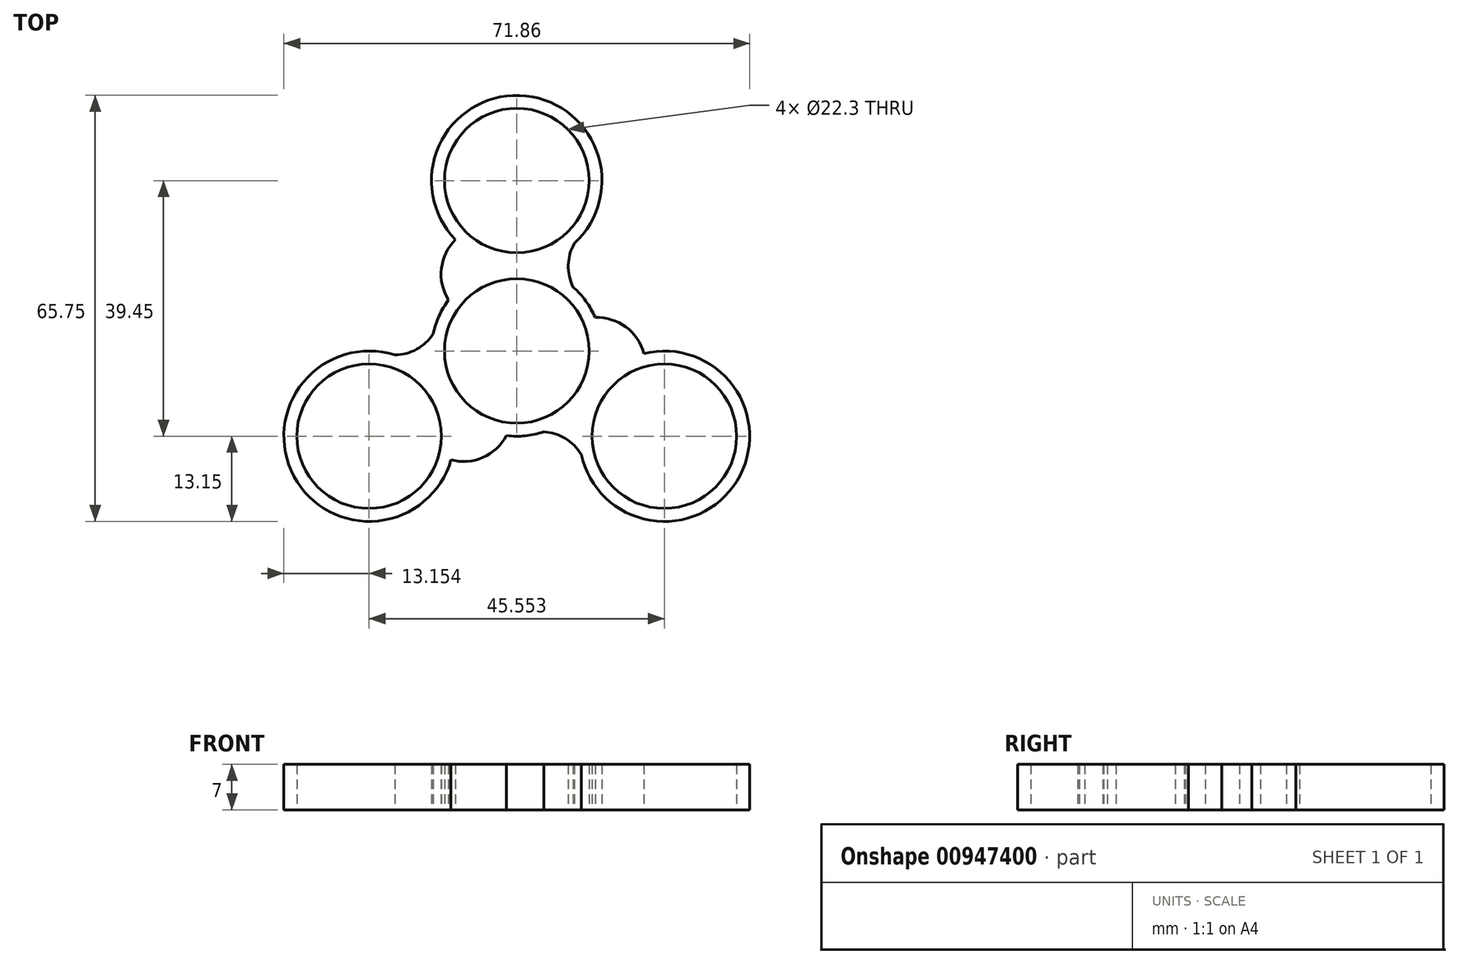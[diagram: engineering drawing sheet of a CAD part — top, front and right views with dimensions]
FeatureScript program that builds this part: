
annotation { "Feature Type Name" : "Feature", "Feature Type Description" : "" }
export const myFeature = defineFeature(function(context is Context, id is Id, definition is map)
    precondition{}
    {
        {
            var Q0;
            Q0=qCreatedBy(makeId("Top.planeOp"),FACE);
            var sketch = newSketch(context, id + "F0", { "sketchPlane" : qUnion([Q0])});
            skCircle(sketch, "E0", {"center": v(0, 0) * mm, "radius": 11.15 * mm});
            skCircle(sketch, "E1.0", {"center": v(0, 0) * mm, "radius": 13.15 * mm});
            skCircle(sketch, "E2", {"center": v(0, 26.3) * mm, "radius": 11.15 * mm});
            skCircle(sketch, "E3.0", {"center": v(0, 26.3) * mm, "radius": 13.15 * mm});
            skArc(sketch, "E4", {"start": v(-9.48, 17.18) * mm, "mid": v(-11.63, 12.72) * mm, "end": v(-10.52, 7.89) * mm});
            skArc(sketch, "E5", {"start": v(8.88, 16.6) * mm, "mid": v(7.96, 13.24) * mm, "end": v(8.72, 9.84) * mm});
            skCircle(sketch, "E6.1.0", {"center": v(-22.78, -13.15) * mm, "radius": 13.15 * mm});
            skCircle(sketch, "E6.1.1", {"center": v(-22.78, -13.15) * mm, "radius": 11.15 * mm});
            skArc(sketch, "E6.1.2", {"start": v(-18.81, -0.61) * mm, "mid": v(-15.45, 0.27) * mm, "end": v(-12.88, 2.63) * mm});
            skArc(sketch, "E6.1.3", {"start": v(-10.14, -16.8) * mm, "mid": v(-5.2, -16.43) * mm, "end": v(-1.57, -13.06) * mm});
            skCircle(sketch, "E6.2.0", {"center": v(22.78, -13.15) * mm, "radius": 13.15 * mm});
            skCircle(sketch, "E6.2.1", {"center": v(22.78, -13.15) * mm, "radius": 11.15 * mm});
            skArc(sketch, "E6.2.2", {"start": v(9.94, -15.99) * mm, "mid": v(7.49, -13.51) * mm, "end": v(4.16, -12.47) * mm});
            skArc(sketch, "E6.2.3", {"start": v(19.62, -0.39) * mm, "mid": v(16.83, 3.71) * mm, "end": v(12.1, 5.17) * mm});
            skSolve(sketch);
        }
        {
            var Q0;
            Q0 = qSketchRegion(id + "F0", true);
            extrude(context, id + "F1", {"entities" : qUnion([Q0]), "depth" : 7 * mm, "offsetDistance" : 25 * mm});
        }
    });
